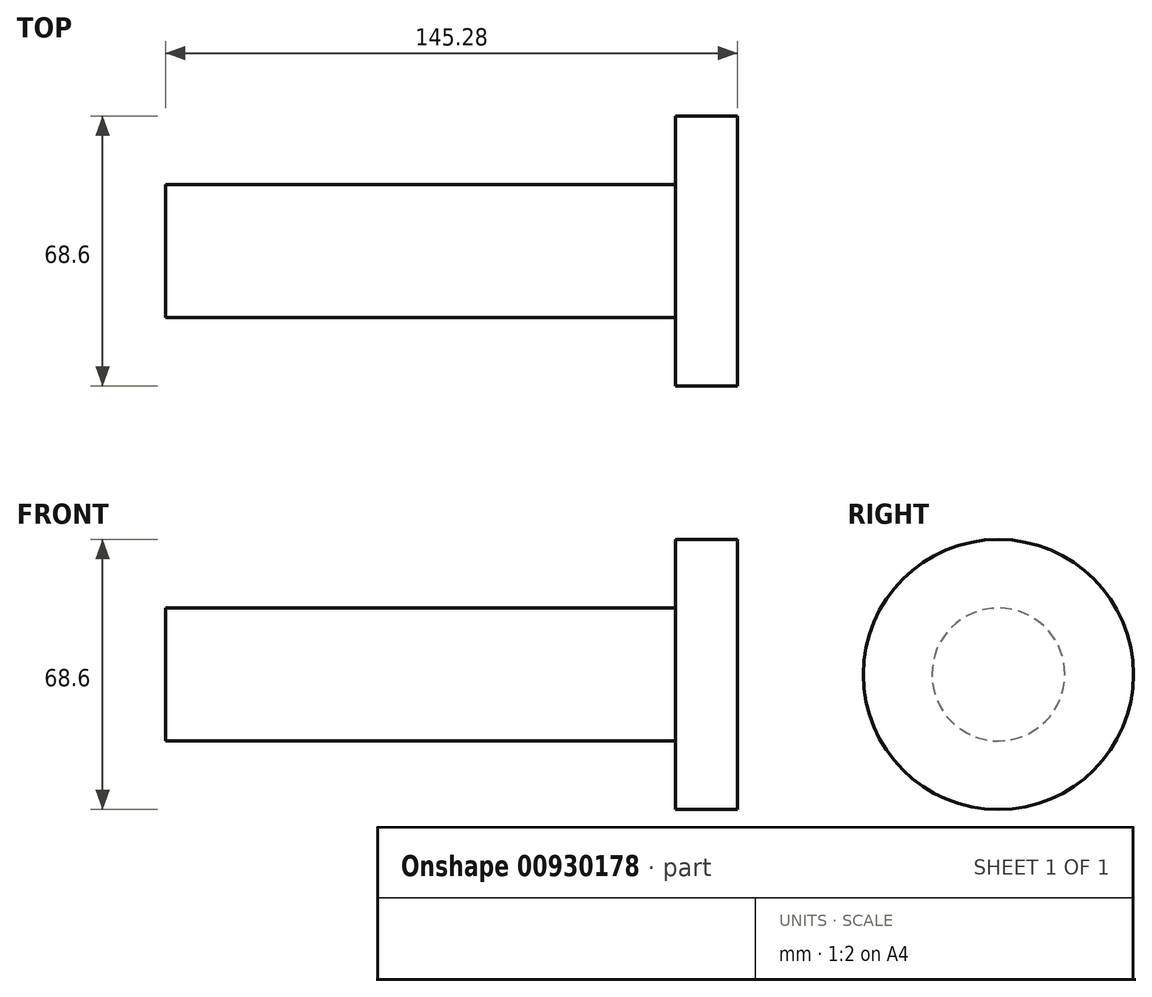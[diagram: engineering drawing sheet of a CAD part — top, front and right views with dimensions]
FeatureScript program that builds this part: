
annotation { "Feature Type Name" : "Feature", "Feature Type Description" : "" }
export const myFeature = defineFeature(function(context is Context, id is Id, definition is map)
    precondition{}
    {
        {
            var Q0;
            Q0=qCreatedBy(makeId("Top.planeOp"),FACE);
            var sketch = newSketch(context, id + "F0", { "sketchPlane" : qUnion([Q0])});
            skLineSegment(sketch, "E0.bottom", {"start": v(-129.58, 16.88) * mm, "end": v(0, 16.88) * mm});
            skLineSegment(sketch, "E0.top", {"start": v(-129.58, 0) * mm, "end": v(0, 0) * mm});
            skLineSegment(sketch, "E0.left", {"start": v(-129.58, 16.88) * mm, "end": v(-129.58, 0) * mm});
            skLineSegment(sketch, "E0.right", {"start": v(0, 16.88) * mm, "end": v(0, 0) * mm});
            skLineSegment(sketch, "E1.bottom", {"start": v(0, 0) * mm, "end": v(15.7, 0) * mm});
            skLineSegment(sketch, "E1.top", {"start": v(0, 34.3) * mm, "end": v(15.7, 34.3) * mm});
            skLineSegment(sketch, "E1.left", {"start": v(0, 0) * mm, "end": v(0, 34.3) * mm});
            skLineSegment(sketch, "E1.right", {"start": v(15.7, 0) * mm, "end": v(15.7, 34.3) * mm});
            skSolve(sketch);
        }
        {
            var Q0;
            {var subQ0=sQuery(id+"F0.wireOp",EDGE,"E0.bottom");Q0=makeQuery(id+"F0.imprint","IMPRINT",FACE,{"disambiguationData":[TD([[makeQuery(id+"F0.imprint","IMPRINT",EDGE,{"derivedFrom":subQ0}),-1.0]])]});}
            var Q1;
            {var subQ3=sQuery(id+"F0.wireOp",EDGE,"E1.bottom");Q1=makeQuery(id+"F0.imprint","IMPRINT",FACE,{"disambiguationData":[TD([[makeQuery(id+"F0.imprint","IMPRINT",EDGE,{"derivedFrom":subQ3}),1.0]])]});}
            var Q2;
            Q2=sQuery(id+"F0.wireOp",EDGE,"E0.top");
            revolve(context, id + "F1", {"surfaceOperationType" : NewSurfaceOperationType.NEW, "entities" : qUnion([Q0, Q1]), "axis" : qUnion([Q2]), "revolveType" : RevolveType.FULL});
        }
    });
